# Revit family: Waterless-2903-Santa-Fe
name_source: partatom
category: Plumbing Fixtures
revit_build: Autodesk Revit 2016 (Build: 20150220_1215(x64)
units: mm (PartAtom-declared; Revit-internal decimal feet)

## family parameters
Cut with Voids When Loaded = No
Host = Face
Part Type = Normal
Room Calculation Point = No
Round Connector Dimension = Use Diameter
Shared = No

## types (2) — shared parameters
CW Connection = No
Description = Waterless Co. Inc. No-Flush™ urinal Model #2903 Santa Fe™, wall hung, made of High
Performance Composite material (HPC) for commercial and residential use.
Dimensions = 14.0 x 19.5 x 14.0 in (356 x 483 x 356 mm)
HW Connection = No
Manufacturer = Waterless Co.
Material = High Performance Composite (HPC)
Model = #2903
Type Comments = Commercial and Residential Use
Type Image = <None>
URL = www.waterless.com
Vent Connection = No
Waste Connection = Yes
Weight = 16 lbs (7.3 kg)

## per-type parameters (varying)
| type | Default Elevation |
| Standard | 2' - 0" |
| ADA Compliant | 1' - 5" |

## geometry (parser evidence)
native form markers: Sweep x3
no freeform markers — native parametric forms only
